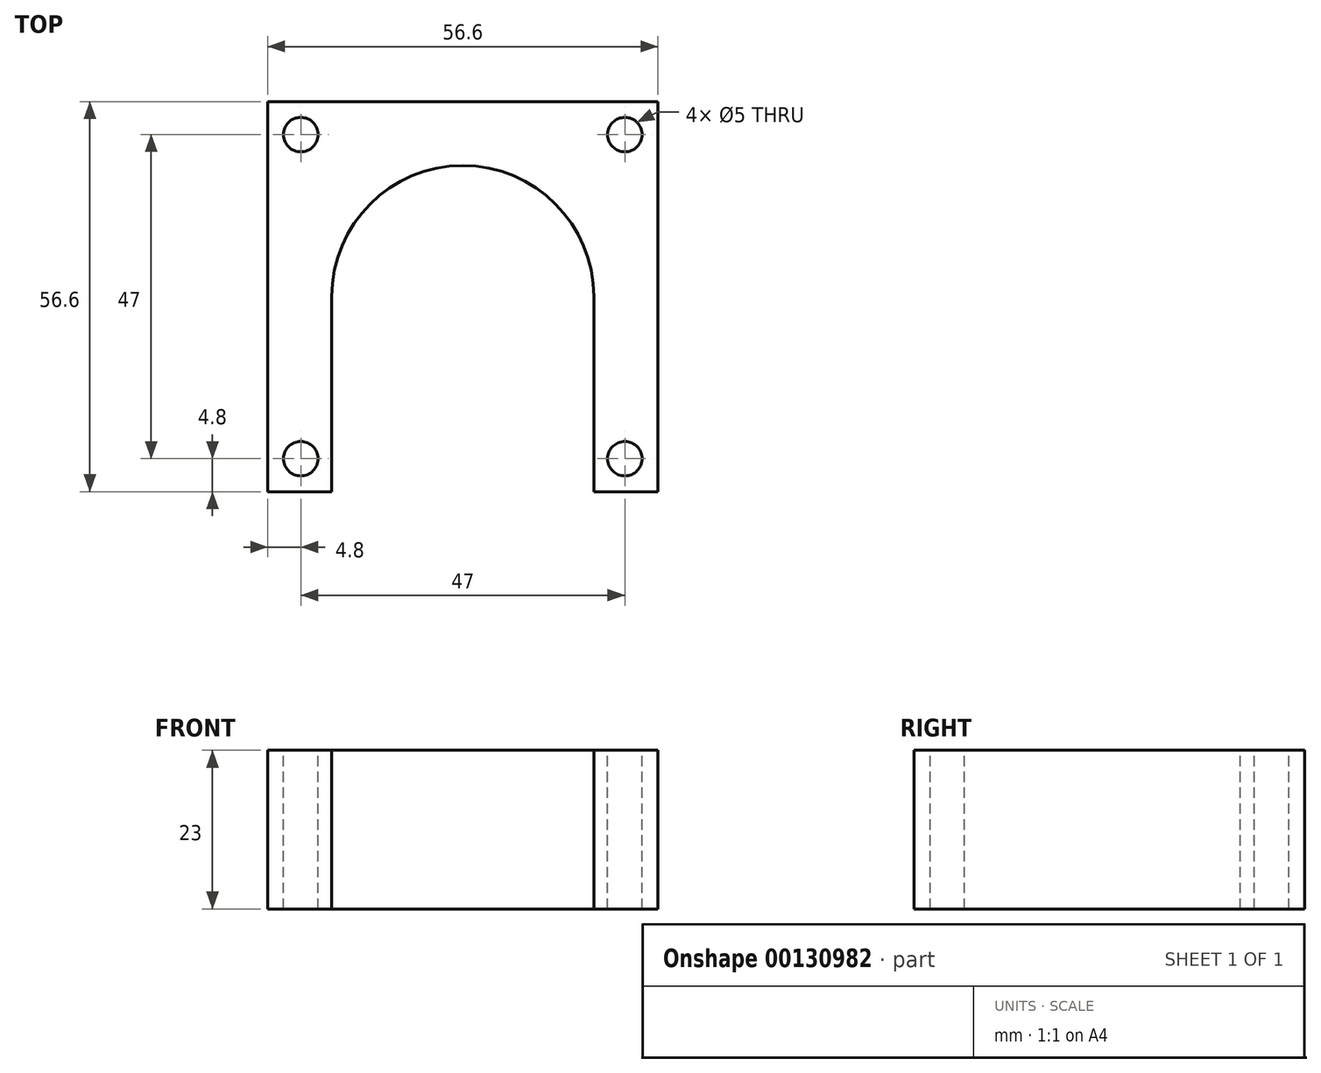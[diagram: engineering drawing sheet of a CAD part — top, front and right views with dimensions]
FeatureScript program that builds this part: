
annotation { "Feature Type Name" : "Feature", "Feature Type Description" : "" }
export const myFeature = defineFeature(function(context is Context, id is Id, definition is map)
    precondition{}
    {
        {
            var Q0;
            Q0=qCreatedBy(makeId("Top.planeOp"),FACE);
            var sketch = newSketch(context, id + "F0", { "sketchPlane" : qUnion([Q0])});
            skLineSegment(sketch, "E0.bottom", {"start": v(0, 0) * mm, "end": v(56.6, 0) * mm});
            skLineSegment(sketch, "E0.top", {"start": v(0, 56.6) * mm, "end": v(56.6, 56.6) * mm});
            skLineSegment(sketch, "E0.left", {"start": v(0, 0) * mm, "end": v(0, 56.6) * mm});
            skLineSegment(sketch, "E0.right", {"start": v(56.6, 0) * mm, "end": v(56.6, 56.6) * mm});
            skSolve(sketch);
        }
        {
            var Q0;
            Q0=makeQuery(id+"F0.imprint","IMPRINT",FACE,{"disambiguationData":[TD([[makeQuery(id+"F0.imprint","IMPRINT",EDGE,{"derivedFrom":sQuery(id+"F0.wireOp",EDGE,"E0.bottom")}),1.0]])]});
            extrude(context, id + "F1", {"entities" : qUnion([Q0]), "depth" : 23 * mm});
        }
        {
            var Q0;
            Q0=makeQuery(id+"F1.opExtrude","CAP_FACE",FACE,{"disambiguationData":[OSD([sQuery(id+"F0.wireOp",EDGE,"E0.bottom"),sQuery(id+"F0.wireOp",EDGE,"E0.top"),sQuery(id+"F0.wireOp",EDGE,"E0.left"),sQuery(id+"F0.wireOp",EDGE,"E0.right")])],"isStart":false});
            var sketch = newSketch(context, id + "F2", { "sketchPlane" : qUnion([Q0])});
            skCircle(sketch, "E1", {"center": v(28.3, 28.3) * mm, "radius": 19 * mm});
            skLineSegment(sketch, "E2", {"start": v(0, 28.3) * mm, "end": v(56.6, 28.3) * mm});
            skPoint(sketch, "E2.endSnap0", {"position": v(56.6, 28.3) * mm});
            skLineSegment(sketch, "E3", {"start": v(28.3, 56.6) * mm, "end": v(28.3, 0) * mm});
            skLineSegment(sketch, "E4.bottom", {"start": v(9.3, 28.3) * mm, "end": v(47.3, 28.3) * mm});
            skLineSegment(sketch, "E4.top", {"start": v(9.3, 0) * mm, "end": v(47.3, 0) * mm});
            skLineSegment(sketch, "E4.left", {"start": v(9.3, 28.3) * mm, "end": v(9.3, 0) * mm});
            skLineSegment(sketch, "E4.right", {"start": v(47.3, 28.3) * mm, "end": v(47.3, 0) * mm});
            skSolve(sketch);
        }
        {
            var Q0;
            Q0 = qSketchRegion(id + "F2", true);
            var Q1;
            Q1=makeQuery(id+"F1.opExtrude","CAP_FACE",FACE,{"disambiguationData":[OSD([sQuery(id+"F0.wireOp",EDGE,"E0.bottom"),sQuery(id+"F0.wireOp",EDGE,"E0.top"),sQuery(id+"F0.wireOp",EDGE,"E0.left"),sQuery(id+"F0.wireOp",EDGE,"E0.right")])],"isStart":true});
            extrude(context, id + "F3", {"entities" : qUnion([Q0]), "operationType" : NewBodyOperationType.REMOVE, "endBound" : BoundingType.UP_TO_SURFACE, "oppositeDirection" : true, "endBoundEntityFace" : qUnion([Q1]), "depth" : 25 * mm});
        }
        {
            var Q0;
            Q0=makeQuery(id+"F1.opExtrude","CAP_FACE",FACE,{"disambiguationData":[OSD([sQuery(id+"F0.wireOp",EDGE,"E0.bottom"),sQuery(id+"F0.wireOp",EDGE,"E0.top"),sQuery(id+"F0.wireOp",EDGE,"E0.left"),sQuery(id+"F0.wireOp",EDGE,"E0.right")])],"isStart":false});
            var sketch = newSketch(context, id + "F4", { "sketchPlane" : qUnion([Q0])});
            skLineSegment(sketch, "E5.bottom", {"start": v(4.8, 51.8) * mm, "end": v(51.8, 51.8) * mm});
            skLineSegment(sketch, "E5.top", {"start": v(4.8, 4.8) * mm, "end": v(51.8, 4.8) * mm});
            skLineSegment(sketch, "E5.left", {"start": v(4.8, 51.8) * mm, "end": v(4.8, 4.8) * mm});
            skLineSegment(sketch, "E5.right", {"start": v(51.8, 51.8) * mm, "end": v(51.8, 4.8) * mm});
            skLineSegment(sketch, "E6", {"start": v(4.8, 51.8) * mm, "end": v(0, 51.8) * mm});
            skLineSegment(sketch, "E7", {"start": v(4.8, 51.8) * mm, "end": v(4.8, 56.6) * mm});
            skLineSegment(sketch, "E8", {"start": v(51.8, 4.8) * mm, "end": v(51.8, 0) * mm});
            skLineSegment(sketch, "E9", {"start": v(51.8, 4.8) * mm, "end": v(56.6, 4.8) * mm});
            skSolve(sketch);
        }
        {
            var Q0;
            Q0=sQuery(id+"F4.wireOp",VERTEX,"E7.start");
            var Q1;
            Q1=sQuery(id+"F4.wireOp",VERTEX,"E5.right.start");
            var Q2;
            Q2=sQuery(id+"F4.wireOp",VERTEX,"E8.start");
            var Q3;
            Q3=sQuery(id+"F4.wireOp",VERTEX,"E5.left.end");
            var Q4;
            Q4=makeQuery(id+"F1.opExtrude","SWEPT_BODY",BODY,{"disambiguationData":[OSD([sQuery(id+"F0.wireOp",EDGE,"E0.bottom"),sQuery(id+"F0.wireOp",EDGE,"E0.top"),sQuery(id+"F0.wireOp",EDGE,"E0.left"),sQuery(id+"F0.wireOp",EDGE,"E0.right")])]});
            hole(context, id + "F5", {"style" : HoleStyle.SIMPLE, "endStyle" : HoleEndStyle.THROUGH, "holeDiameter" : 5 * mm, "locations" : qUnion([Q0, Q1, Q2, Q3]), "scope" : qUnion([Q4]), "isTappedThrough" : true});
        }
    });
